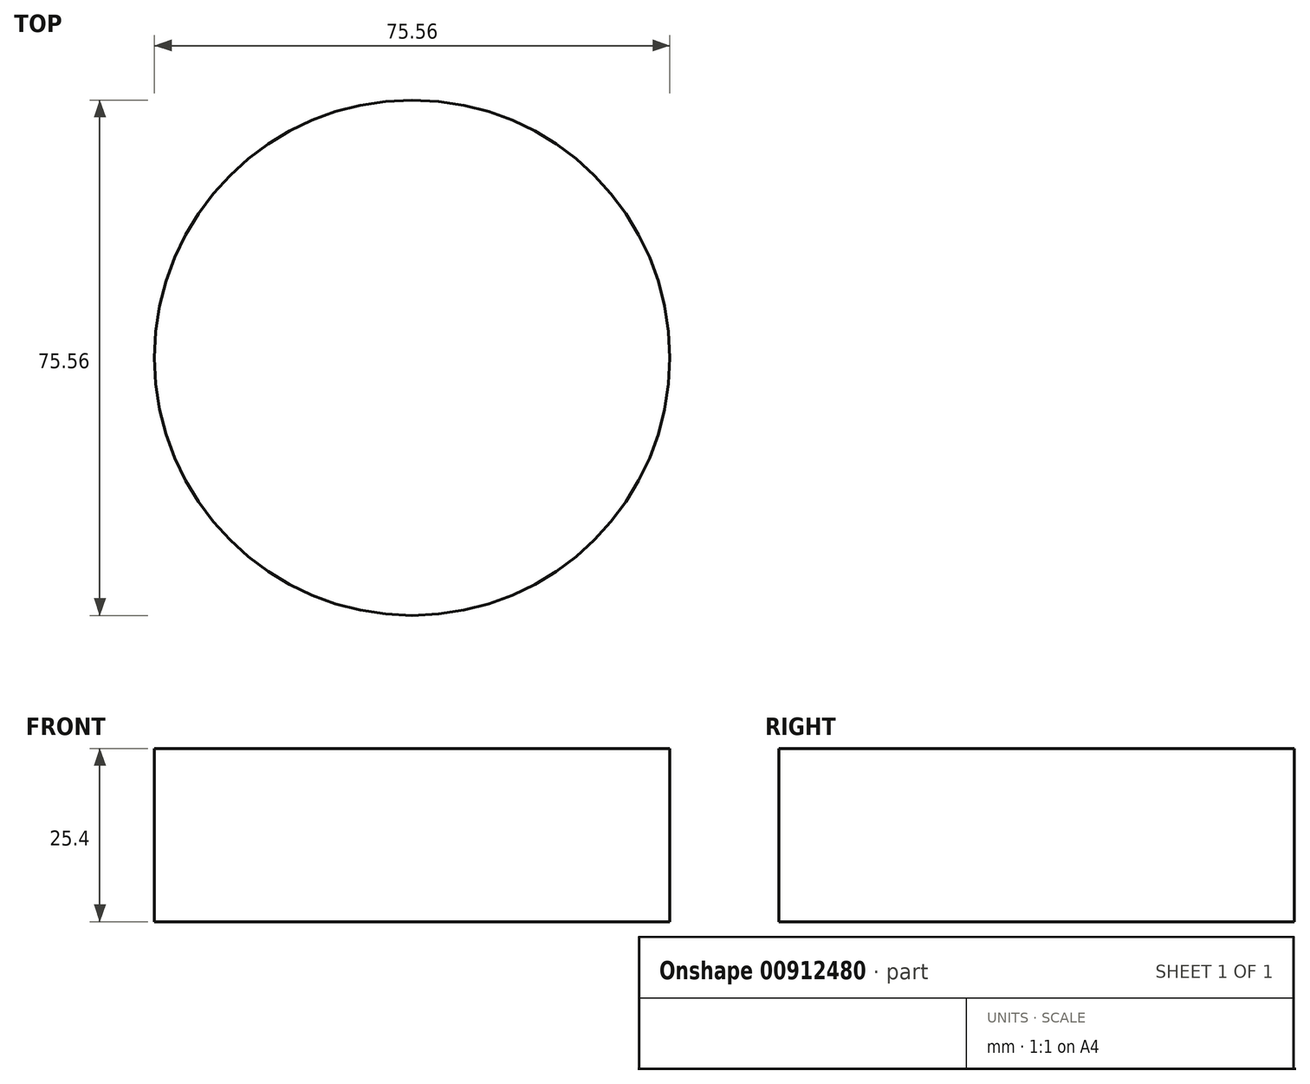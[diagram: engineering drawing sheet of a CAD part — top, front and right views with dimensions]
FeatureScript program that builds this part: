
annotation { "Feature Type Name" : "Feature", "Feature Type Description" : "" }
export const myFeature = defineFeature(function(context is Context, id is Id, definition is map)
    precondition{}
    {
        {
            var Q0;
            Q0=qCreatedBy(makeId("Top.planeOp"),FACE);
            var sketch = newSketch(context, id + "F0", { "sketchPlane" : qUnion([Q0])});
            skCircle(sketch, "E0", {"center": v(0, 0) * mm, "radius": 37.78 * mm});
            skSolve(sketch);
        }
        {
            var Q0;
            Q0=makeQuery(id+"F0.imprint","IMPRINT",FACE,{"disambiguationData":[TD([[makeQuery(id+"F0.imprint","IMPRINT",EDGE,{"derivedFrom":sQuery(id+"F0.wireOp",EDGE,"E0")}),1.0]])]});
            extrude(context, id + "F1", {"entities" : qUnion([Q0]), "depth" : 25.4 * mm, "offsetDistance" : 25.4 * mm});
        }
    });
